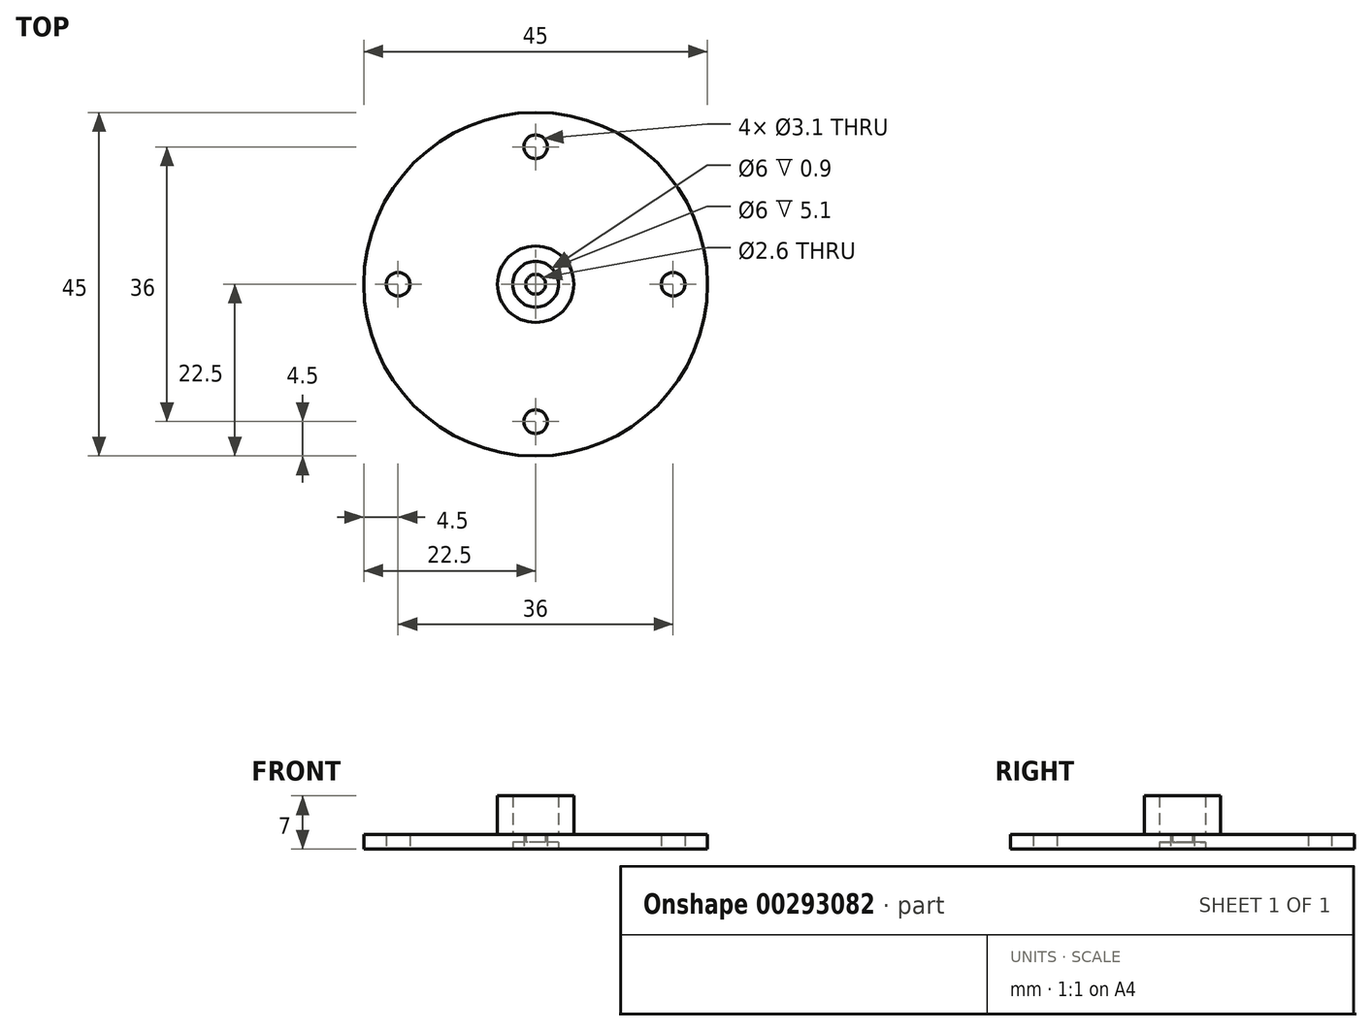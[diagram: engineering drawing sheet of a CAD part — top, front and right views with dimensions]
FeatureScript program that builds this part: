
annotation { "Feature Type Name" : "Feature", "Feature Type Description" : "" }
export const myFeature = defineFeature(function(context is Context, id is Id, definition is map)
    precondition{}
    {
        {
            var Q0;
            Q0=qCreatedBy(makeId("Top.planeOp"),FACE);
            var sketch = newSketch(context, id + "F0", { "sketchPlane" : qUnion([Q0])});
            skCircle(sketch, "E0", {"center": v(0, 0) * mm, "radius": 22.5 * mm});
            skCircle(sketch, "E1", {"center": v(0, 0) * mm, "radius": 5 * mm});
            skCircle(sketch, "E2", {"center": v(0, 0) * mm, "radius": 3 * mm});
            skCircle(sketch, "E3", {"center": v(0, 0) * mm, "radius": 1.3 * mm});
            skLineSegment(sketch, "E4", {"start": v(0, 0) * mm, "end": v(0, 22.5) * mm, "construction": true});
            skCircle(sketch, "E5", {"center": v(0, 18) * mm, "radius": 1.55 * mm});
            skCircle(sketch, "E6.1.0", {"center": v(-18, 0) * mm, "radius": 1.55 * mm});
            skCircle(sketch, "E6.2.0", {"center": v(0, -18) * mm, "radius": 1.55 * mm});
            skCircle(sketch, "E6.3.0", {"center": v(18, 0) * mm, "radius": 1.55 * mm});
            skSolve(sketch);
        }
        {
            var Q0;
            Q0=makeQuery(id+"F0.imprint","IMPRINT",FACE,{"disambiguationData":[TD([[makeQuery(id+"F0.imprint","IMPRINT",EDGE,{"derivedFrom":sQuery(id+"F0.wireOp",EDGE,"E0")}),1.0]])]});
            extrude(context, id + "F1", {"entities" : qUnion([Q0]), "depth" : 1.9 * mm});
        }
        {
            var Q0;
            Q0=makeQuery(id+"F0.imprint","IMPRINT",FACE,{"disambiguationData":[TD([[makeQuery(id+"F0.imprint","IMPRINT",EDGE,{"derivedFrom":sQuery(id+"F0.wireOp",EDGE,"E1")}),1.0]])]});
            extrude(context, id + "F2", {"entities" : qUnion([Q0]), "operationType" : NewBodyOperationType.ADD, "depth" : 7 * mm});
        }
        {
            var Q0;
            Q0=makeQuery(id+"F0.imprint","IMPRINT",FACE,{"disambiguationData":[TD([[makeQuery(id+"F0.imprint","IMPRINT",EDGE,{"derivedFrom":sQuery(id+"F0.wireOp",EDGE,"E2")}),1.0]])]});
            extrude(context, id + "F3", {"entities" : qUnion([Q0]), "operationType" : NewBodyOperationType.ADD, "depth" : 1.9 * mm, "hasSecondDirection" : true, "secondDirectionOppositeDirection" : false, "secondDirectionDepth" : .9 * mm});
        }
    });
